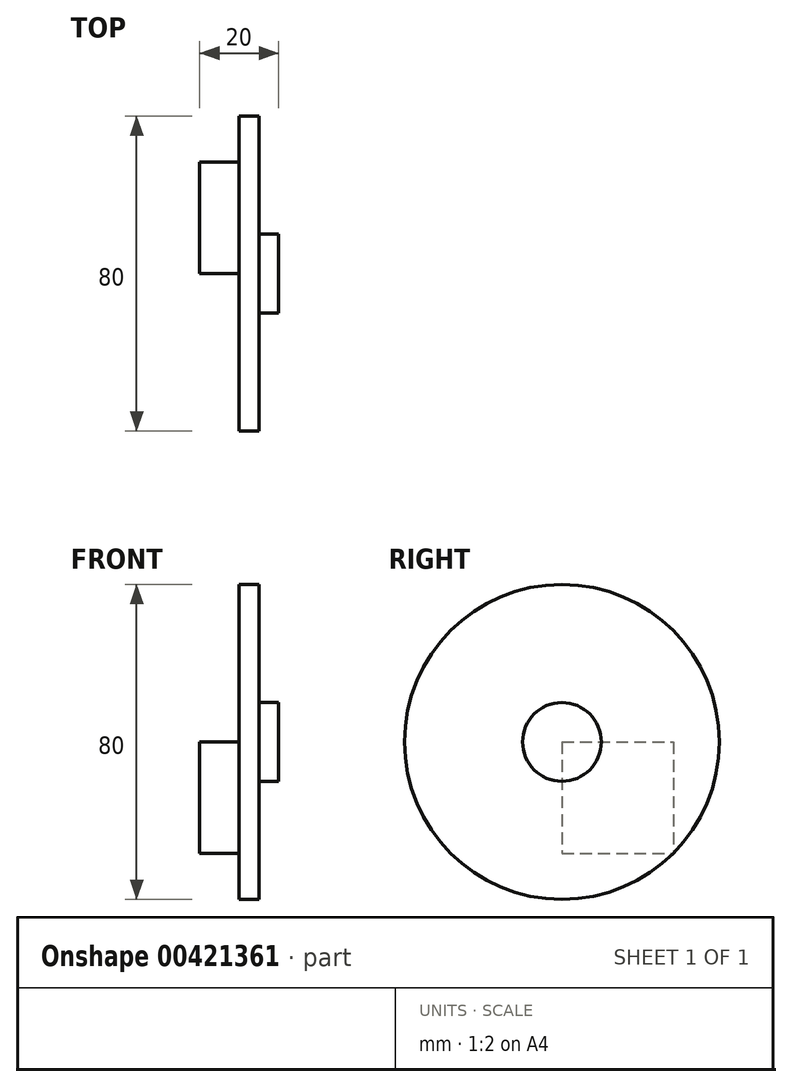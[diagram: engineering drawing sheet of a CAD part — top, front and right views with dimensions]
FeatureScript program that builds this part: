
annotation { "Feature Type Name" : "Feature", "Feature Type Description" : "" }
export const myFeature = defineFeature(function(context is Context, id is Id, definition is map)
    precondition{}
    {
        {
            var Q0;
            Q0=qCreatedBy(makeId("Right.planeOp"),FACE);
            var sketch = newSketch(context, id + "F0", { "sketchPlane" : qUnion([Q0])});
            skCircle(sketch, "E0", {"center": v(0, 0) * mm, "radius": 10 * mm});
            skCircle(sketch, "E1", {"center": v(0, 0) * mm, "radius": 40 * mm});
            skSolve(sketch);
        }
        {
            var Q0;
            Q0 = qSketchRegion(id + "F0", true);
            var Q1;
            Q1=makeQuery(id+"F0.imprint","IMPRINT",FACE,{"disambiguationData":[TD([[makeQuery(id+"F0.imprint","IMPRINT",EDGE,{"derivedFrom":sQuery(id+"F0.wireOp",EDGE,"E0")}),1.0]])]});
            extrude(context, id + "F1", {"entities" : qUnion([Q0, Q1]), "oppositeDirection" : true, "depth" : 5 * mm});
        }
        {
            var Q0;
            Q0=makeQuery(id+"F0.imprint","IMPRINT",FACE,{"disambiguationData":[TD([[makeQuery(id+"F0.imprint","IMPRINT",EDGE,{"derivedFrom":sQuery(id+"F0.wireOp",EDGE,"E0")}),1.0]])]});
            extrude(context, id + "F2", {"entities" : qUnion([Q0]), "operationType" : NewBodyOperationType.ADD, "depth" : 5 * mm});
        }
        {
            var Q0;
            Q0=makeQuery(id+"F1.opExtrude","CAP_FACE",FACE,{"disambiguationData":[OSD([sQuery(id+"F0.wireOp",EDGE,"E1")])],"isStart":false});
            var sketch = newSketch(context, id + "F3", { "sketchPlane" : qUnion([Q0])});
            skPoint(sketch, "E2.middle", {"position": v(0, 0) * mm});
            skLineSegment(sketch, "E3.bottom", {"start": v(0, 0) * mm, "end": v(-28.28, 0) * mm});
            skLineSegment(sketch, "E3.top", {"start": v(0, -28.28) * mm, "end": v(-28.28, -28.28) * mm});
            skLineSegment(sketch, "E3.left", {"start": v(0, 0) * mm, "end": v(0, -28.28) * mm});
            skLineSegment(sketch, "E3.right", {"start": v(-28.28, 0) * mm, "end": v(-28.28, -28.28) * mm});
            skSolve(sketch);
        }
        {
            var Q0;
            Q0=makeQuery(id+"F3.imprint","IMPRINT",FACE,{"disambiguationData":[TD([[makeQuery(id+"F3.imprint","IMPRINT",EDGE,{"derivedFrom":sQuery(id+"F3.wireOp",EDGE,"E3.bottom")}),1.0]])]});
            extrude(context, id + "F4", {"entities" : qUnion([Q0]), "operationType" : NewBodyOperationType.ADD, "depth" : 10 * mm});
        }
    });
